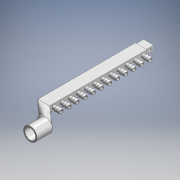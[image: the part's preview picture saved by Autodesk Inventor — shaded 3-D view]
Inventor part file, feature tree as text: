
AUTODESK INVENTOR PART (.ipt)
format: ipt  version: 2018 (Build 220112000, 112)  size: 422,400 bytes
history: native  units: in
note: dims shown in document units (in); Inventor stores cm internally (conversion verified against a paired STEP export)
features: other x10, extrude x4, pattern_linear x2, loft x2, fillet x1, projected_geometry x1
ambient origin geometry x8: Origin, YZ Plane, XZ Plane, XY Plane, X Axis, Y Axis, Z Axis, Center Point
bodies: Body1 (feature_tree)
feature tree (20):
  other  "CrossSection1"
  other  "Silicone Fitting Plane"
  other  "Cap Plane"
  other  "Base Sketch"
  extrude  "Base"  Depth=0.0197in
  other  "Silicone Fitting"
  extrude  "Airflow Cut"  Depth=0.0591in
  extrude  "Coupling"  Depth=0.0591in
  pattern_linear  "Airflow Cut Repetition"  Spacing1=0.0591in  [1 undecoded]
  pattern_linear  "Rectangular Pattern7"  Spacing1=0.0197in  [1 undecoded]
  other  "Mouthpiece Adapter Plane"
  other  "Mouthpiece Adapter Loft To"
  loft  "Mouthpiece Adapter Outer"
  loft  "Moutpiece Adapter Inner"
  extrude  "Mouthpiece"  Depth=4.9606in
  fillet  "Fillet1"  [1 undecoded]
  other  "Silicone Fitting Sketch"
  other  "Airflow Cut Sketch"
  projected_geometry  "Projected Loop7"
  other  "Coupling Sketch"
note: 3 required parameter values undecoded (feature->parameter linkage not recoverable at this tier; creation-order binding heuristic only, values carry confidence <= 0.55)
